# Revit family: Electronics_Amplifiers_Biamp_Voltera_A-300.2
name_source: partatom
category: Communication Devices
units: mm (PartAtom-declared; Revit-internal decimal feet)

## family parameters
Cut with Voids When Loaded = No
Host = Face
Maintain Annotation Orientation = No
OmniClass Number = 23.85.10.11.14.14.17
OmniClass Title = Sound Amplifiers
Part Type = Normal
Room Calculation Point = No
Round Connector Dimension = Use Diameter
Shared = No

## types (1)
- A-300.2
    Apparent Load = 300 VA
    Channel separation (crosstalk at 1 kHz) = >75 dB
    Connector Description = 100-240 VAC, 50/60 Hz
    Control/monitoring IO = Mute all channels (input);Health (output);Sleep mode status (output);Sleep mode (input)
    Cooling = Variable speed fans, front to back airfow
    Default Elevation = 48 "
    Depth = 11 "
    Description = Voltera® A Series Compact 2 Channel, 300 Amplifier Models
    Frequency response (20 - 20000 Hz, 8 ohm, unweighted) = +/-0.5 dB
    Gain for 4 ohm = 26 dB
    Gain for 70 / 100 V = 35.2 / 38.2 dB
    Gain for 8 ohm = 29 dB
    Gain trim (default 0 dB) = In addition to reducing the gain down to -infnity, it can boost the gain and power by up to 3 dB
    Height = 2 "
    High pass flter = 70 Hz 12 dB/octave (on/of)
    Housing Material = Biamp - Metal - Black
    Humidity = 0-95% non-condensing
    Included accessories = Rack solution for single/tandem 19 1 RU mount; Brackets for mounting under table/on wall/under ceiling
    Input impedance (balanced) = 8 kohm
    Input sensitivity (for all Mode options) = +4 dBu (1.23 Vrms)
    Manufacturer = Biamp
    Max Power Consumption = 300 W
    Max input level = +24 dBu
    Mode switch / ch. (4 Ω / 8 Ω / 70 V / 100 V) = Defnes the gain and the limiter thresholds
    Model = A-300.2
    Nom Double Unit Left Rack Mount = Double Unit Left Rack Mount
    Nom Double Unit Right Rack Mount = Double Unit Right Rack Mount
    Nom Freestanding Mount = Freestanding Mount
    Nom Single Unit Rack Mount = Single Unit Rack Mount
    Nom Surface Mount = Surface Mount
    Number of Poles = 1
    Power Factor = 1
    Product Documentation Link = https://downloads.biamp.com
    Product Page URL = https://www.biamp.com
    Product data url = https://bimobject.com
    Signal level indicator = Signal level and limiter action
    Signal to Noise ratio (8 ohm) = >103 dBA
    THD+N (1 kHz, 1 dB below clip) = <0.008%
    THD+N (20 - 20000 Hz for 1 W into 8 ohm) = <0.5%
    Temperature Range = 32-104°F (0-40°C)
    URL = https://www.biamp.com
    Version = 1
    Voltage = 240 V
    Weight = 6.10 lb
    Width = 9 "

## geometry (parser evidence)
native form markers: Sweep x19
no freeform markers — native parametric forms only
